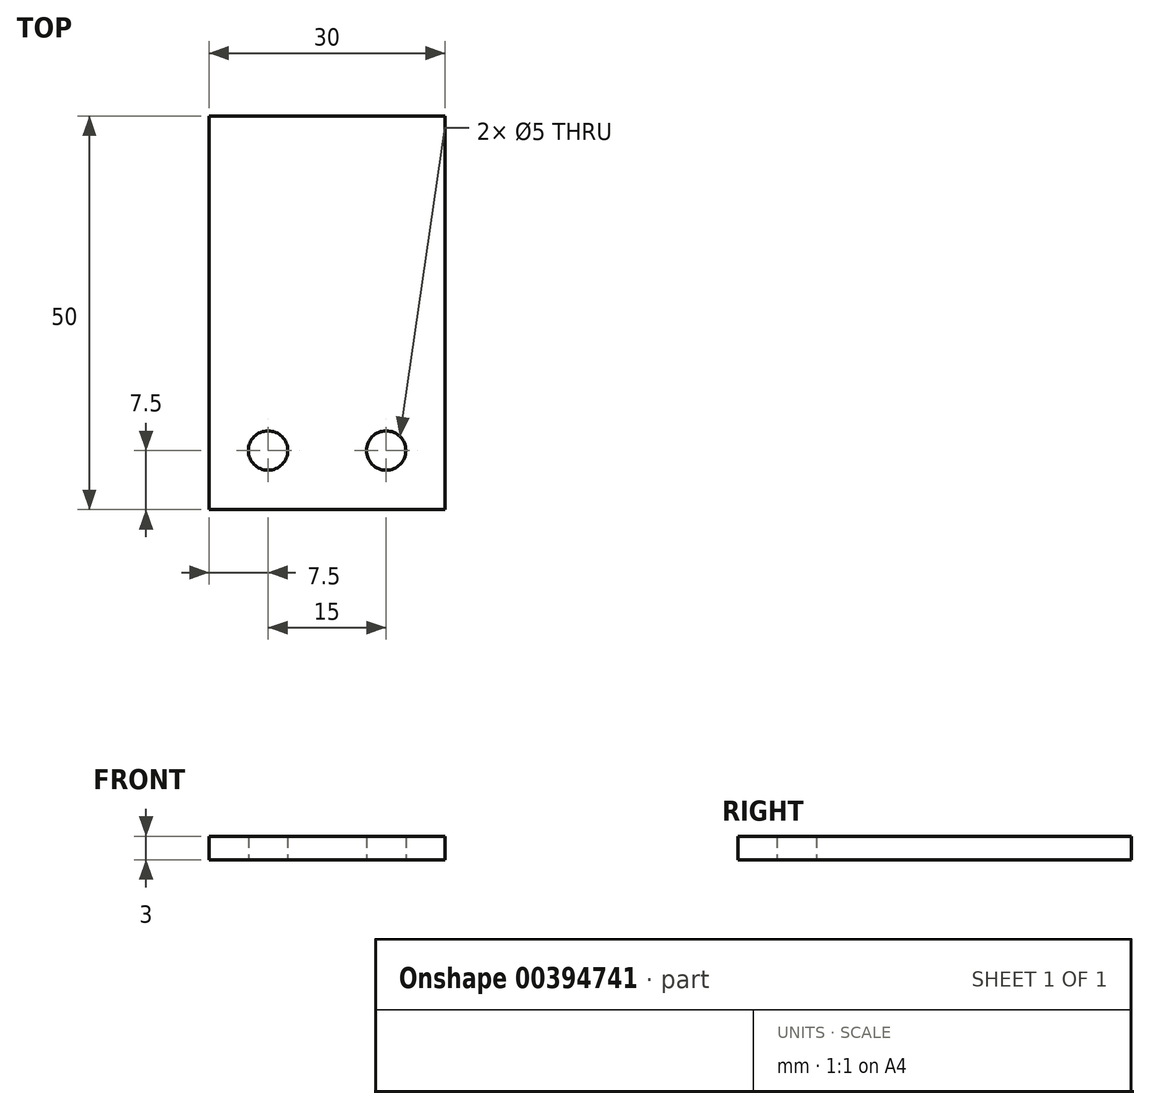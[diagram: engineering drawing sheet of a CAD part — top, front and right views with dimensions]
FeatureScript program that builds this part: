
annotation { "Feature Type Name" : "Feature", "Feature Type Description" : "" }
export const myFeature = defineFeature(function(context is Context, id is Id, definition is map)
    precondition{}
    {
        {
            var Q0;
            Q0=qCreatedBy(makeId("Top.planeOp"),FACE);
            var sketch = newSketch(context, id + "F0", { "sketchPlane" : qUnion([Q0])});
            skLineSegment(sketch, "E0.bottom", {"start": v(-15, 25) * mm, "end": v(15, 25) * mm});
            skLineSegment(sketch, "E0.top", {"start": v(-15, -25) * mm, "end": v(15, -25) * mm});
            skLineSegment(sketch, "E0.left", {"start": v(-15, 25) * mm, "end": v(-15, -25) * mm});
            skLineSegment(sketch, "E0.right", {"start": v(15, 25) * mm, "end": v(15, -25) * mm});
            skPoint(sketch, "E0.middle", {"position": v(0, 0) * mm});
            skCircle(sketch, "E1", {"center": v(-7.5, -17.5) * mm, "radius": 2.5 * mm});
            skCircle(sketch, "E2", {"center": v(7.5, -17.5) * mm, "radius": 2.5 * mm});
            skLineSegment(sketch, "E3", {"start": v(7.5, -20) * mm, "end": v(7.5, -25) * mm, "construction": true});
            skLineSegment(sketch, "E4", {"start": v(10, -17.5) * mm, "end": v(15, -17.5) * mm, "construction": true});
            skLineSegment(sketch, "E5", {"start": v(-10, -17.5) * mm, "end": v(-15, -17.5) * mm, "construction": true});
            skSolve(sketch);
        }
        {
            var Q0;
            Q0=makeQuery(id+"F0.imprint","IMPRINT",FACE,{"disambiguationData":[TD([[makeQuery(id+"F0.imprint","IMPRINT",EDGE,{"derivedFrom":sQuery(id+"F0.wireOp",EDGE,"E0.bottom")}),-1.0]])]});
            extrude(context, id + "F1", {"entities" : qUnion([Q0]), "depth" : 3 * mm});
        }
    });
